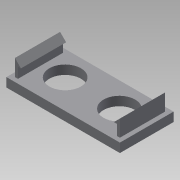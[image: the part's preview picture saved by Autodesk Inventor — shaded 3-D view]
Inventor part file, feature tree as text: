
AUTODESK INVENTOR PART (.ipt)
format: ipt  version: 2015 SP1 (Build 190203100, 203)  size: 146,944 bytes
history: native  units: mm
features: extrude x4, sketch x4, projected_geometry x2
ambient origin geometry x8: Origin, YZ Plane, XZ Plane, XY Plane, X Axis, Y Axis, Z Axis, Center Point
bodies: Solid1 (feature_tree)
feature tree (10):
  extrude  "Extrusion1"  Depth=3.0mm
  extrude  "Extrusion2"  Depth=32.85mm
  extrude  "Extrusion3"  Depth=15.0mm
  extrude  "Extrusion4"  Depth=3.0mm
  sketch  "Sketch1"  dims[d0=3.0mm d1=0.0mm d2=10.5mm]
  sketch  "Sketch2"  dims[d3=32.85mm d4=32.85mm]
  projected_geometry  "Projected Loop1"
  sketch  "Sketch3"  dims[d5=16.425mm d6=15.0mm]
  sketch  "Sketch4"  dims[d7=15.0mm d8=12.5mm d9=18.0mm d12=9.0mm d13=9.0mm d14=10.5mm d15=6.75mm d16=6.75mm d17=1.0mm d18=1.0mm d19=6.5mm d20=0.0mm d21=45.0deg d22=2.0mm d23=45.0deg d24=15.0mm d25=0.0mm d26=2.0mm d27=45.0deg d28=2.0mm d29=45.0deg d30=2.0mm d31=135.0deg d32=180.0deg d33=3.0mm d34=0.0mm d35=2.0mm]
  projected_geometry  "Projected Loop2"
